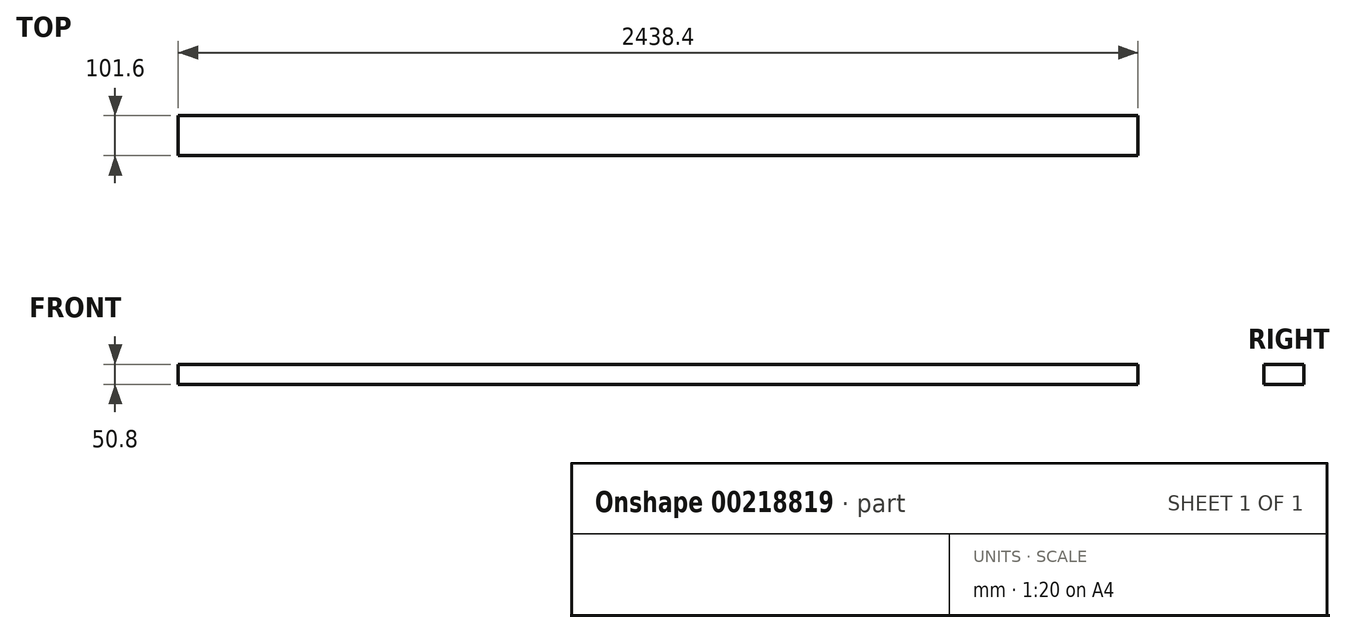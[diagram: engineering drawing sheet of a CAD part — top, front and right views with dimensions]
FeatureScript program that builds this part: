
annotation { "Feature Type Name" : "Feature", "Feature Type Description" : "" }
export const myFeature = defineFeature(function(context is Context, id is Id, definition is map)
    precondition{}
    {
        {
            var Q0;
            Q0=qCreatedBy(makeId("Top.planeOp"),FACE);
            var sketch = newSketch(context, id + "F0", { "sketchPlane" : qUnion([Q0])});
            skLineSegment(sketch, "E0.bottom", {"start": v(0, 0) * mm, "end": v(2438.4, 0) * mm});
            skLineSegment(sketch, "E0.top", {"start": v(0, -101.6) * mm, "end": v(2438.4, -101.6) * mm});
            skLineSegment(sketch, "E0.left", {"start": v(0, 0) * mm, "end": v(0, -101.6) * mm});
            skLineSegment(sketch, "E0.right", {"start": v(2438.4, 0) * mm, "end": v(2438.4, -101.6) * mm});
            skSolve(sketch);
        }
        {
            var Q0;
            Q0=makeQuery(id+"F0.imprint","IMPRINT",FACE,{"disambiguationData":[TD([[makeQuery(id+"F0.imprint","IMPRINT",EDGE,{"derivedFrom":sQuery(id+"F0.wireOp",EDGE,"E0.bottom")}),-1.0]])]});
            extrude(context, id + "F1", {"entities" : qUnion([Q0]), "depth" : 50.8 * mm});
        }
    });
